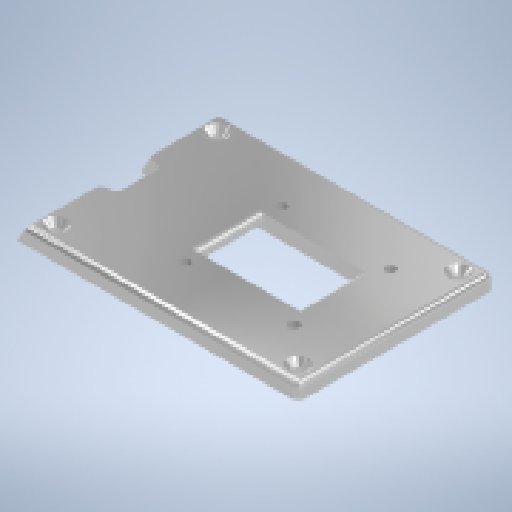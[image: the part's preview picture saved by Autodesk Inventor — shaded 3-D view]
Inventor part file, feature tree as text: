
AUTODESK INVENTOR PART (.ipt)
format: ipt  version: 2025 (Build 290162010, 162A)  size: 295,424 bytes
history: native  units: mm
features: sketch x7, fillet x4, hole x2, extrude x1, sweep x1, loft x1
ambient origin geometry x8: Origin, YZ Plane, XZ Plane, XY Plane, X Axis, Y Axis, Z Axis, Center Point
bodies: Volumenkörper1 (feature_tree)
feature tree (16):
  extrude  "Extrusion1"  Depth=5.0mm
  hole  "hebel"  [1 undecoded]
  fillet  "Rundung2"  Radius=90.0mm
  fillet  "Rundung3"  Radius=25.0mm
  sketch  "Skizze10"  dims[d61=5.0mm d62=15.0mm]
  sweep  "Sweeping2"
  hole  "Bohrung5"  [1 undecoded]
  fillet  "Rundung5"  Radius=4.0mm
  loft  "Erhebung1"
  fillet  "Rundung6"  [1 undecoded]
  sketch  "Skizze1"  dims[d6=5.0mm d7=0.0mm d15=36.0mm]
  sketch  "Skizze3"  dims[d16=32.0mm d17=18.0mm]
  sketch  "Skizze8"  dims[d18=3.242mm d19=8.0mm d20=4.5mm d21=2.0mm d22=90.0deg d23=8.0mm d24=20.594885mm d59=90.0mm d60=25.0mm]
  sketch  "Skizze11"  dims[d63=2.0mm d64=2.0mm d65=4.0mm]
  sketch  "Skizze12"  dims[d66=3.2mm d67=6.0mm d68=7.0mm d69=2.0mm d70=90.0deg d71=8.0mm d72=20.594885mm d79=60.0deg d80=0.0mm d81=0.0mm]
  sketch  "Skizze14"  dims[d82=2.0mm d83=20.0mm d85=11.82mm d86=15.0mm d87=1.0mm d88=20.0mm d89=13.64mm d90=0.0mm d91=90.0deg d92=0.0mm d93=90.0deg d94=2.0mm]
note: 3 required parameter values undecoded (feature->parameter linkage not recoverable at this tier; creation-order binding heuristic only, values carry confidence <= 0.55)
